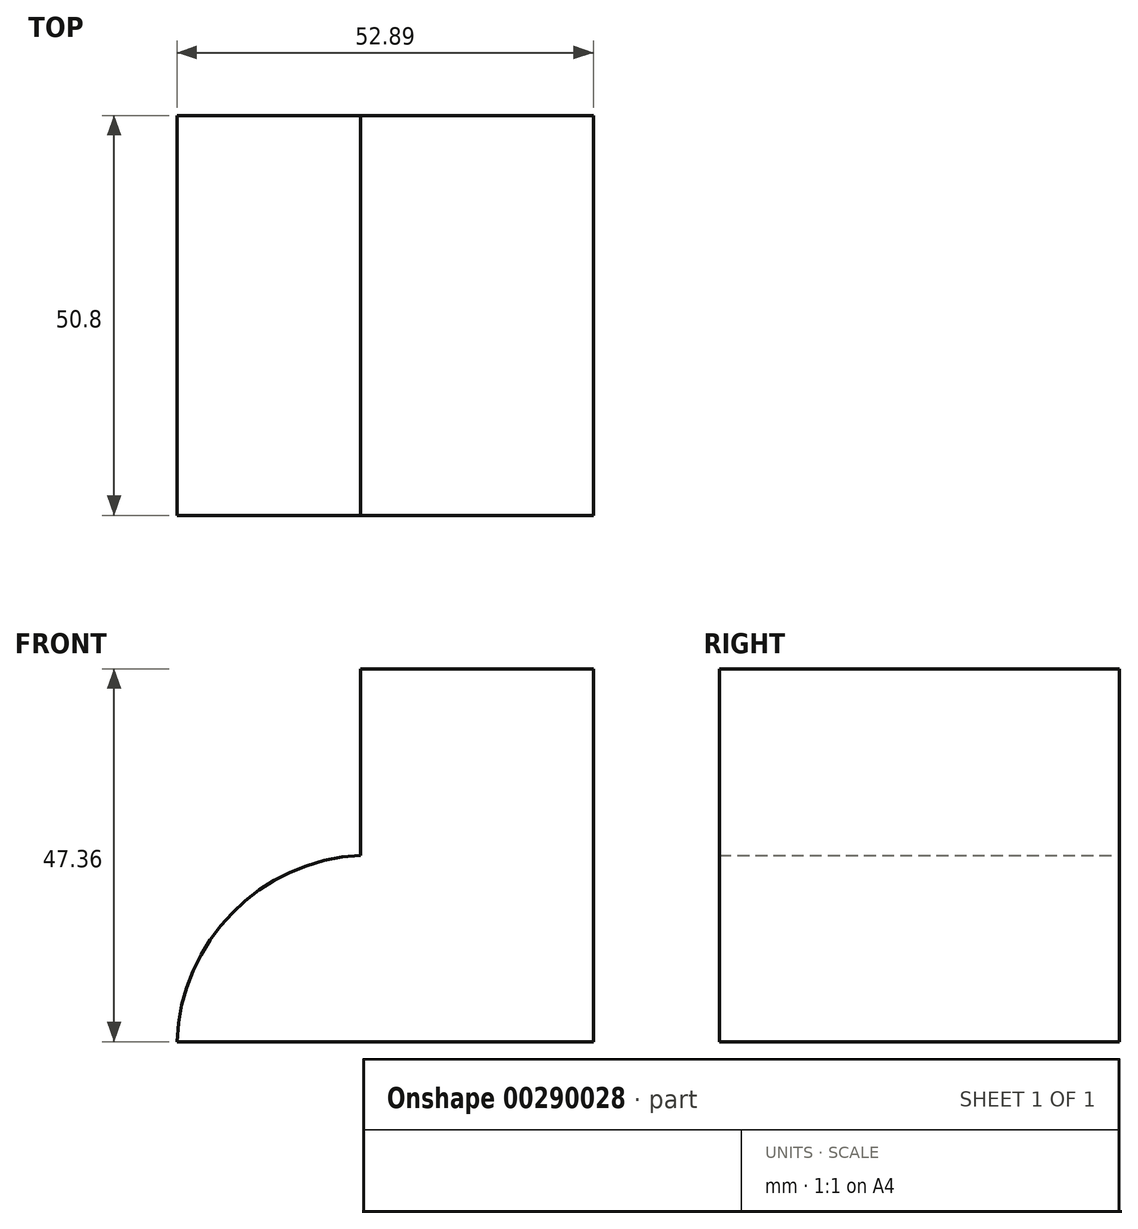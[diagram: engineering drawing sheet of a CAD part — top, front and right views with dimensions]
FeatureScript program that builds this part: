
annotation { "Feature Type Name" : "Feature", "Feature Type Description" : "" }
export const myFeature = defineFeature(function(context is Context, id is Id, definition is map)
    precondition{}
    {
        {
            var Q0;
            Q0=qCreatedBy(makeId("Front.planeOp"),FACE);
            var sketch = newSketch(context, id + "F0", { "sketchPlane" : qUnion([Q0])});
            skLineSegment(sketch, "E0.bottom", {"start": v(0, 0) * mm, "end": v(-29.6, 0) * mm});
            skLineSegment(sketch, "E0.top", {"start": v(0, 47.36) * mm, "end": v(-29.6, 47.36) * mm});
            skLineSegment(sketch, "E0.left", {"start": v(0, 0) * mm, "end": v(0, 47.36) * mm});
            skLineSegment(sketch, "E0.right", {"start": v(-29.6, 23.68) * mm, "end": v(-29.6, 47.36) * mm});
            skArc(sketch, "E1", {"start": v(-29.6, 23.68) * mm, "mid": v(-45.85, 16.37) * mm, "end": v(-52.9, 0) * mm});
            skLineSegment(sketch, "E2", {"start": v(-52.9, 0) * mm, "end": v(-29.6, 0) * mm});
            skSolve(sketch);
        }
        {
            var Q0;
            Q0=makeQuery(id+"F0.imprint","IMPRINT",FACE,{"disambiguationData":[TD([[makeQuery(id+"F0.imprint","IMPRINT",EDGE,{"derivedFrom":sQuery(id+"F0.wireOp",EDGE,"E0.bottom")}),-1.0]])]});
            extrude(context, id + "F1", {"entities" : qUnion([Q0]), "depth" : 50.8 * mm});
        }
    });
